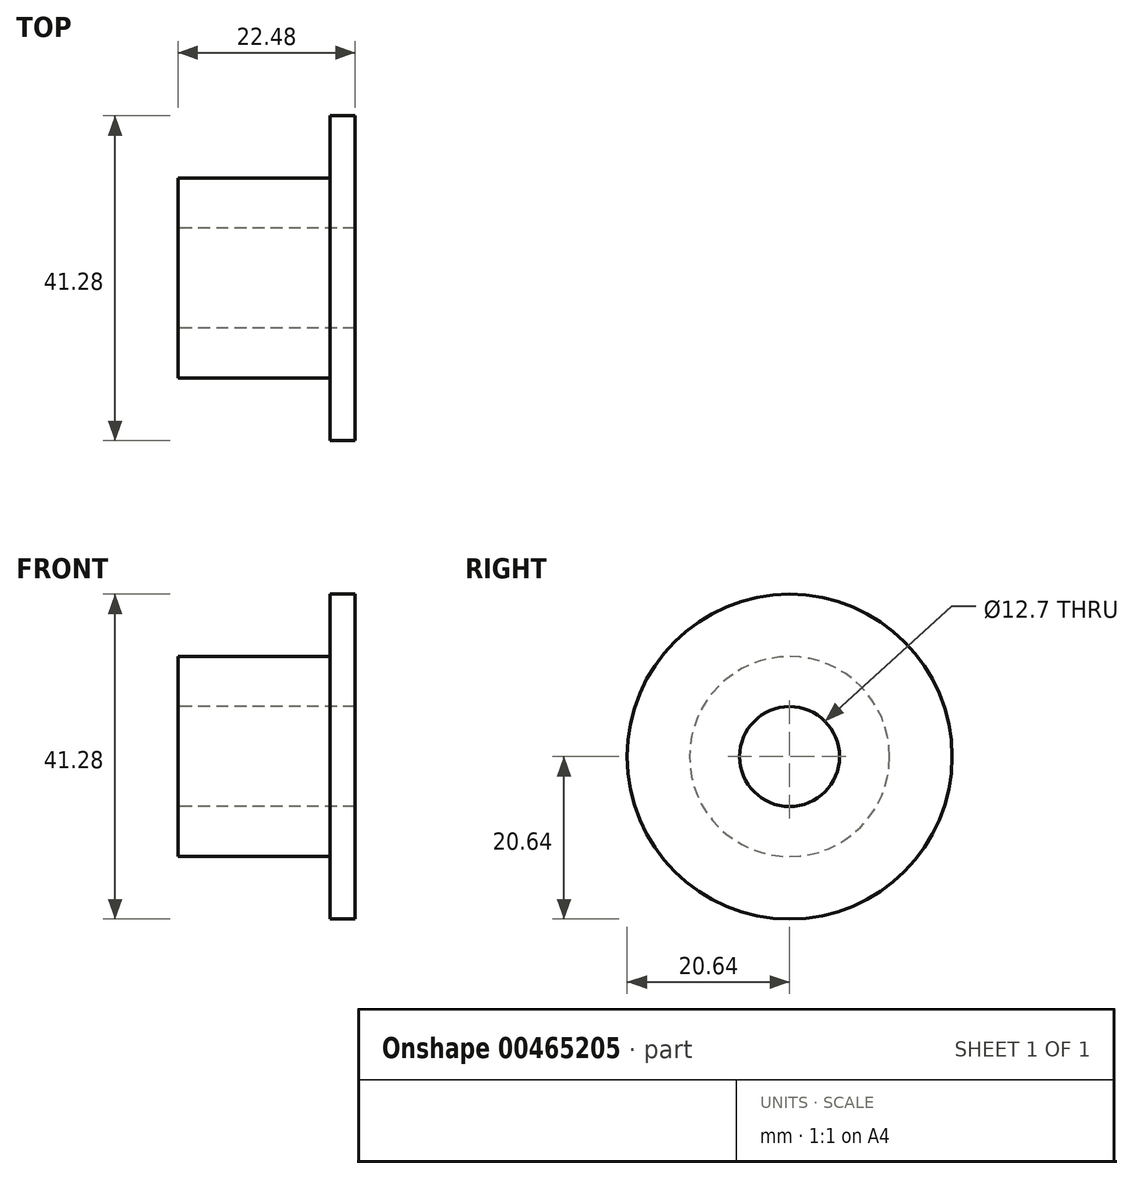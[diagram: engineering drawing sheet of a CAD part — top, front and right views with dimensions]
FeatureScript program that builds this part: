
annotation { "Feature Type Name" : "Feature", "Feature Type Description" : "" }
export const myFeature = defineFeature(function(context is Context, id is Id, definition is map)
    precondition{}
    {
        {
            var Q0;
            Q0=qCreatedBy(makeId("Right.planeOp"),FACE);
            var sketch = newSketch(context, id + "F0", { "sketchPlane" : qUnion([Q0])});
            skCircle(sketch, "E0", {"center": v(0, 0) * mm, "radius": 20.64 * mm});
            skCircle(sketch, "E1", {"center": v(0, 0) * mm, "radius": 12.7 * mm});
            skCircle(sketch, "E2", {"center": v(0, 0) * mm, "radius": 6.35 * mm});
            skSolve(sketch);
        }
        {
            var Q0;
            Q0=makeQuery(id+"F0.imprint","IMPRINT",FACE,{"disambiguationData":[TD([[makeQuery(id+"F0.imprint","IMPRINT",EDGE,{"derivedFrom":sQuery(id+"F0.wireOp",EDGE,"E0")}),1.0]])]});
            var Q1;
            Q1=makeQuery(id+"F0.imprint","IMPRINT",FACE,{"disambiguationData":[TD([[makeQuery(id+"F0.imprint","IMPRINT",EDGE,{"derivedFrom":sQuery(id+"F0.wireOp",EDGE,"E1")}),1.0]])]});
            extrude(context, id + "F1", {"entities" : qUnion([Q0, Q1]), "depth" : 3.17 * mm});
        }
        {
            var Q0;
            Q0=makeQuery(id+"F0.imprint","IMPRINT",FACE,{"disambiguationData":[TD([[makeQuery(id+"F0.imprint","IMPRINT",EDGE,{"derivedFrom":sQuery(id+"F0.wireOp",EDGE,"E1")}),1.0]])]});
            extrude(context, id + "F2", {"entities" : qUnion([Q0]), "operationType" : NewBodyOperationType.ADD, "oppositeDirection" : true, "depth" : 19.3 * mm});
        }
    });
